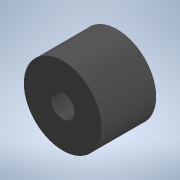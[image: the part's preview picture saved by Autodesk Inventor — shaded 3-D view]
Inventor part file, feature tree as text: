
AUTODESK INVENTOR PART (.ipt)
format: ipt  version: 2021.5 (Build 255421000, 421)  size: 93,184 bytes
history: native  units: mm
features: other x1, extrude x1, sketch x1
ambient origin geometry x8: Origin, YZ Plane, XZ Plane, XY Plane, X Axis, Y Axis, Z Axis, Center Point
bodies: Body1 (feature_tree)
feature tree (3):
  other  "Sólido1"
  extrude  "Extrusión1"  Depth=10.0mm
  sketch  "Boceto1"  dims[d0=3.0mm d1=10.0mm d2=7.0mm d3=0.0mm]
